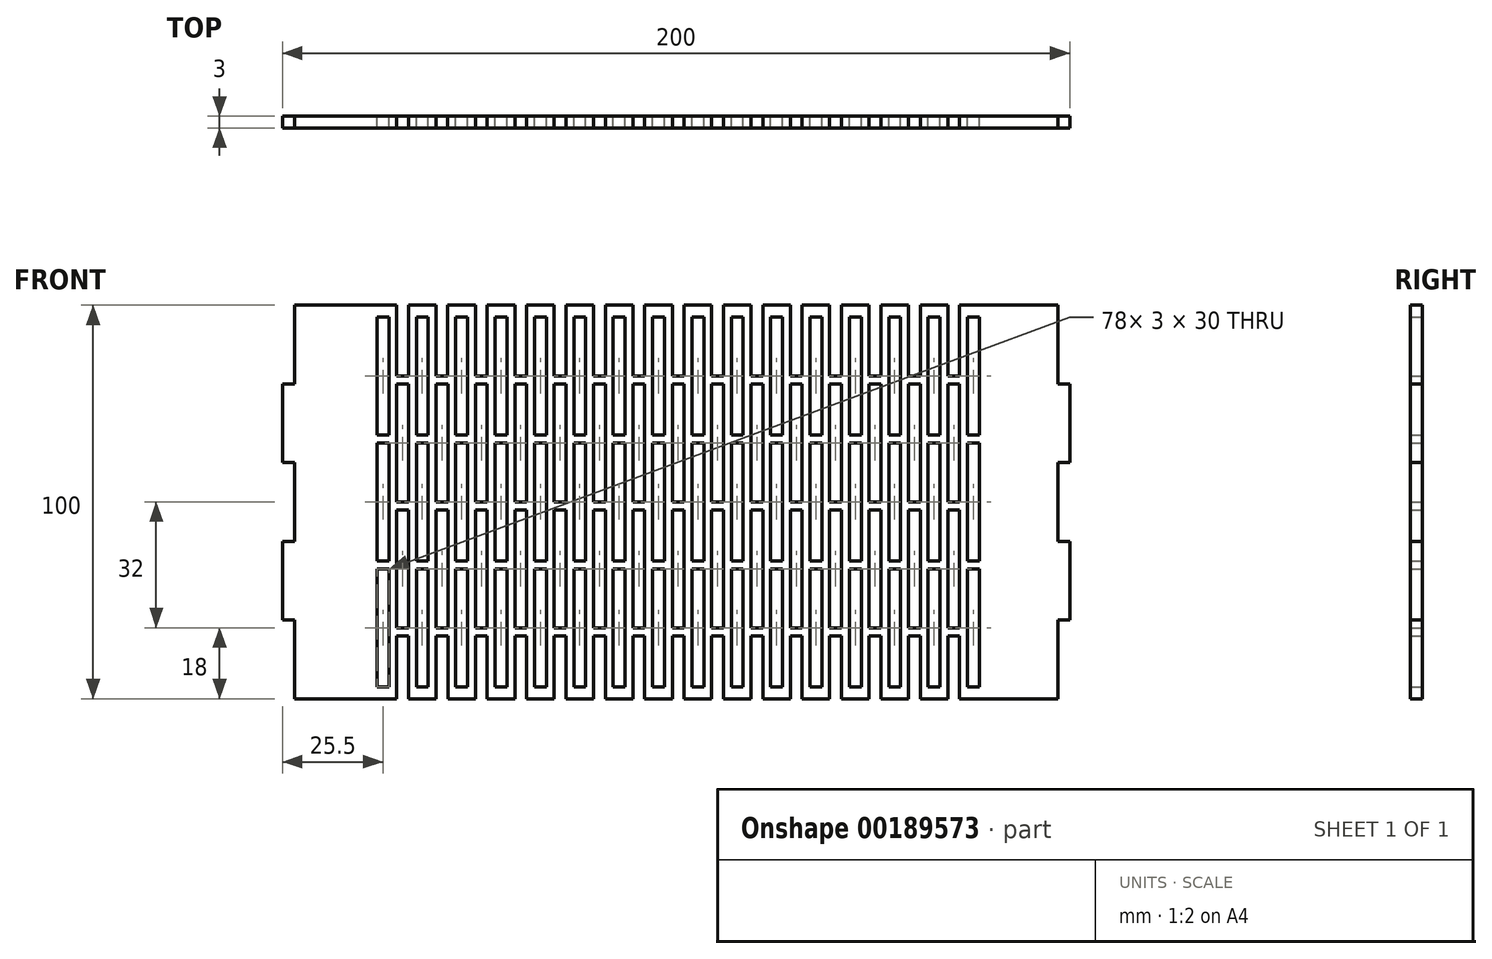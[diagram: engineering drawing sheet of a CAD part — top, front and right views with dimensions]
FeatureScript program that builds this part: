
annotation { "Feature Type Name" : "Feature", "Feature Type Description" : "" }
export const myFeature = defineFeature(function(context is Context, id is Id, definition is map)
    precondition{}
    {
        {
            var Q0;
            Q0=qCreatedBy(makeId("Front.planeOp"),FACE);
            var sketch = newSketch(context, id + "F0", { "sketchPlane" : qUnion([Q0])});
            skLineSegment(sketch, "E0.bottom", {"start": v(80, 50) * mm, "end": v(-80, 50) * mm});
            skLineSegment(sketch, "E0.top", {"start": v(80, -50) * mm, "end": v(-80, -50) * mm});
            skLineSegment(sketch, "E0.left", {"start": v(80, 50) * mm, "end": v(80, -50) * mm});
            skLineSegment(sketch, "E0.right", {"start": v(-80, 50) * mm, "end": v(-80, -50) * mm});
            skPoint(sketch, "E0.middle", {"position": v(0, 0) * mm});
            skLineSegment(sketch, "E1.bottom", {"start": v(-76, 47) * mm, "end": v(-73, 47) * mm});
            skLineSegment(sketch, "E1.top", {"start": v(-76, 17) * mm, "end": v(-73, 17) * mm});
            skLineSegment(sketch, "E1.left", {"start": v(-76, 47) * mm, "end": v(-76, 17) * mm});
            skLineSegment(sketch, "E1.right", {"start": v(-73, 47) * mm, "end": v(-73, 17) * mm});
            skLineSegment(sketch, "E2.0.1.0", {"start": v(-76, -15) * mm, "end": v(-73, -15) * mm});
            skLineSegment(sketch, "E2.0.1.1", {"start": v(-76, 15) * mm, "end": v(-76, -15) * mm});
            skLineSegment(sketch, "E2.0.1.2", {"start": v(-73, 15) * mm, "end": v(-73, -15) * mm});
            skLineSegment(sketch, "E2.0.1.3", {"start": v(-76, 15) * mm, "end": v(-73, 15) * mm});
            skLineSegment(sketch, "E2.0.2.0", {"start": v(-76, -47) * mm, "end": v(-73, -47) * mm});
            skLineSegment(sketch, "E2.0.2.1", {"start": v(-76, -17) * mm, "end": v(-76, -47) * mm});
            skLineSegment(sketch, "E2.0.2.2", {"start": v(-73, -17) * mm, "end": v(-73, -47) * mm});
            skLineSegment(sketch, "E2.0.2.3", {"start": v(-76, -17) * mm, "end": v(-73, -17) * mm});
            skLineSegment(sketch, "E2.1.0.0", {"start": v(-66, 17) * mm, "end": v(-63, 17) * mm});
            skLineSegment(sketch, "E2.1.0.1", {"start": v(-66, 47) * mm, "end": v(-66, 17) * mm});
            skLineSegment(sketch, "E2.1.0.2", {"start": v(-63, 47) * mm, "end": v(-63, 17) * mm});
            skLineSegment(sketch, "E2.1.0.3", {"start": v(-66, 47) * mm, "end": v(-63, 47) * mm});
            skLineSegment(sketch, "E2.1.1.0", {"start": v(-66, -15) * mm, "end": v(-63, -15) * mm});
            skLineSegment(sketch, "E2.1.1.1", {"start": v(-66, 15) * mm, "end": v(-66, -15) * mm});
            skLineSegment(sketch, "E2.1.1.2", {"start": v(-63, 15) * mm, "end": v(-63, -15) * mm});
            skLineSegment(sketch, "E2.1.1.3", {"start": v(-66, 15) * mm, "end": v(-63, 15) * mm});
            skLineSegment(sketch, "E2.1.2.0", {"start": v(-66, -47) * mm, "end": v(-63, -47) * mm});
            skLineSegment(sketch, "E2.1.2.1", {"start": v(-66, -17) * mm, "end": v(-66, -47) * mm});
            skLineSegment(sketch, "E2.1.2.2", {"start": v(-63, -17) * mm, "end": v(-63, -47) * mm});
            skLineSegment(sketch, "E2.1.2.3", {"start": v(-66, -17) * mm, "end": v(-63, -17) * mm});
            skLineSegment(sketch, "E2.2.0.0", {"start": v(-56, 17) * mm, "end": v(-53, 17) * mm});
            skLineSegment(sketch, "E2.2.0.1", {"start": v(-56, 47) * mm, "end": v(-56, 17) * mm});
            skLineSegment(sketch, "E2.2.0.2", {"start": v(-53, 47) * mm, "end": v(-53, 17) * mm});
            skLineSegment(sketch, "E2.2.0.3", {"start": v(-56, 47) * mm, "end": v(-53, 47) * mm});
            skLineSegment(sketch, "E2.2.1.0", {"start": v(-56, -15) * mm, "end": v(-53, -15) * mm});
            skLineSegment(sketch, "E2.2.1.1", {"start": v(-56, 15) * mm, "end": v(-56, -15) * mm});
            skLineSegment(sketch, "E2.2.1.2", {"start": v(-53, 15) * mm, "end": v(-53, -15) * mm});
            skLineSegment(sketch, "E2.2.1.3", {"start": v(-56, 15) * mm, "end": v(-53, 15) * mm});
            skLineSegment(sketch, "E2.2.2.0", {"start": v(-56, -47) * mm, "end": v(-53, -47) * mm});
            skLineSegment(sketch, "E2.2.2.1", {"start": v(-56, -17) * mm, "end": v(-56, -47) * mm});
            skLineSegment(sketch, "E2.2.2.2", {"start": v(-53, -17) * mm, "end": v(-53, -47) * mm});
            skLineSegment(sketch, "E2.2.2.3", {"start": v(-56, -17) * mm, "end": v(-53, -17) * mm});
            skLineSegment(sketch, "E2.3.0.0", {"start": v(-46, 17) * mm, "end": v(-43, 17) * mm});
            skLineSegment(sketch, "E2.3.0.1", {"start": v(-46, 47) * mm, "end": v(-46, 17) * mm});
            skLineSegment(sketch, "E2.3.0.2", {"start": v(-43, 47) * mm, "end": v(-43, 17) * mm});
            skLineSegment(sketch, "E2.3.0.3", {"start": v(-46, 47) * mm, "end": v(-43, 47) * mm});
            skLineSegment(sketch, "E2.3.1.0", {"start": v(-46, -15) * mm, "end": v(-43, -15) * mm});
            skLineSegment(sketch, "E2.3.1.1", {"start": v(-46, 15) * mm, "end": v(-46, -15) * mm});
            skLineSegment(sketch, "E2.3.1.2", {"start": v(-43, 15) * mm, "end": v(-43, -15) * mm});
            skLineSegment(sketch, "E2.3.1.3", {"start": v(-46, 15) * mm, "end": v(-43, 15) * mm});
            skLineSegment(sketch, "E2.3.2.0", {"start": v(-46, -47) * mm, "end": v(-43, -47) * mm});
            skLineSegment(sketch, "E2.3.2.1", {"start": v(-46, -17) * mm, "end": v(-46, -47) * mm});
            skLineSegment(sketch, "E2.3.2.2", {"start": v(-43, -17) * mm, "end": v(-43, -47) * mm});
            skLineSegment(sketch, "E2.3.2.3", {"start": v(-46, -17) * mm, "end": v(-43, -17) * mm});
            skLineSegment(sketch, "E2.4.0.0", {"start": v(-36, 17) * mm, "end": v(-33, 17) * mm});
            skLineSegment(sketch, "E2.4.0.1", {"start": v(-36, 47) * mm, "end": v(-36, 17) * mm});
            skLineSegment(sketch, "E2.4.0.2", {"start": v(-33, 47) * mm, "end": v(-33, 17) * mm});
            skLineSegment(sketch, "E2.4.0.3", {"start": v(-36, 47) * mm, "end": v(-33, 47) * mm});
            skLineSegment(sketch, "E2.4.1.0", {"start": v(-36, -15) * mm, "end": v(-33, -15) * mm});
            skLineSegment(sketch, "E2.4.1.1", {"start": v(-36, 15) * mm, "end": v(-36, -15) * mm});
            skLineSegment(sketch, "E2.4.1.2", {"start": v(-33, 15) * mm, "end": v(-33, -15) * mm});
            skLineSegment(sketch, "E2.4.1.3", {"start": v(-36, 15) * mm, "end": v(-33, 15) * mm});
            skLineSegment(sketch, "E2.4.2.0", {"start": v(-36, -47) * mm, "end": v(-33, -47) * mm});
            skLineSegment(sketch, "E2.4.2.1", {"start": v(-36, -17) * mm, "end": v(-36, -47) * mm});
            skLineSegment(sketch, "E2.4.2.2", {"start": v(-33, -17) * mm, "end": v(-33, -47) * mm});
            skLineSegment(sketch, "E2.4.2.3", {"start": v(-36, -17) * mm, "end": v(-33, -17) * mm});
            skLineSegment(sketch, "E2.5.0.0", {"start": v(-26, 17) * mm, "end": v(-23, 17) * mm});
            skLineSegment(sketch, "E2.5.0.1", {"start": v(-26, 47) * mm, "end": v(-26, 17) * mm});
            skLineSegment(sketch, "E2.5.0.2", {"start": v(-23, 47) * mm, "end": v(-23, 17) * mm});
            skLineSegment(sketch, "E2.5.0.3", {"start": v(-26, 47) * mm, "end": v(-23, 47) * mm});
            skLineSegment(sketch, "E2.5.1.0", {"start": v(-26, -15) * mm, "end": v(-23, -15) * mm});
            skLineSegment(sketch, "E2.5.1.1", {"start": v(-26, 15) * mm, "end": v(-26, -15) * mm});
            skLineSegment(sketch, "E2.5.1.2", {"start": v(-23, 15) * mm, "end": v(-23, -15) * mm});
            skLineSegment(sketch, "E2.5.1.3", {"start": v(-26, 15) * mm, "end": v(-23, 15) * mm});
            skLineSegment(sketch, "E2.5.2.0", {"start": v(-26, -47) * mm, "end": v(-23, -47) * mm});
            skLineSegment(sketch, "E2.5.2.1", {"start": v(-26, -17) * mm, "end": v(-26, -47) * mm});
            skLineSegment(sketch, "E2.5.2.2", {"start": v(-23, -17) * mm, "end": v(-23, -47) * mm});
            skLineSegment(sketch, "E2.5.2.3", {"start": v(-26, -17) * mm, "end": v(-23, -17) * mm});
            skLineSegment(sketch, "E2.6.0.0", {"start": v(-16, 17) * mm, "end": v(-13, 17) * mm});
            skLineSegment(sketch, "E2.6.0.1", {"start": v(-16, 47) * mm, "end": v(-16, 17) * mm});
            skLineSegment(sketch, "E2.6.0.2", {"start": v(-13, 47) * mm, "end": v(-13, 17) * mm});
            skLineSegment(sketch, "E2.6.0.3", {"start": v(-16, 47) * mm, "end": v(-13, 47) * mm});
            skLineSegment(sketch, "E2.6.1.0", {"start": v(-16, -15) * mm, "end": v(-13, -15) * mm});
            skLineSegment(sketch, "E2.6.1.1", {"start": v(-16, 15) * mm, "end": v(-16, -15) * mm});
            skLineSegment(sketch, "E2.6.1.2", {"start": v(-13, 15) * mm, "end": v(-13, -15) * mm});
            skLineSegment(sketch, "E2.6.1.3", {"start": v(-16, 15) * mm, "end": v(-13, 15) * mm});
            skLineSegment(sketch, "E2.6.2.0", {"start": v(-16, -47) * mm, "end": v(-13, -47) * mm});
            skLineSegment(sketch, "E2.6.2.1", {"start": v(-16, -17) * mm, "end": v(-16, -47) * mm});
            skLineSegment(sketch, "E2.6.2.2", {"start": v(-13, -17) * mm, "end": v(-13, -47) * mm});
            skLineSegment(sketch, "E2.6.2.3", {"start": v(-16, -17) * mm, "end": v(-13, -17) * mm});
            skLineSegment(sketch, "E2.7.0.0", {"start": v(-6, 17) * mm, "end": v(-3, 17) * mm});
            skLineSegment(sketch, "E2.7.0.1", {"start": v(-6, 47) * mm, "end": v(-6, 17) * mm});
            skLineSegment(sketch, "E2.7.0.2", {"start": v(-3, 47) * mm, "end": v(-3, 17) * mm});
            skLineSegment(sketch, "E2.7.0.3", {"start": v(-6, 47) * mm, "end": v(-3, 47) * mm});
            skLineSegment(sketch, "E2.7.1.0", {"start": v(-6, -15) * mm, "end": v(-3, -15) * mm});
            skLineSegment(sketch, "E2.7.1.1", {"start": v(-6, 15) * mm, "end": v(-6, -15) * mm});
            skLineSegment(sketch, "E2.7.1.2", {"start": v(-3, 15) * mm, "end": v(-3, -15) * mm});
            skLineSegment(sketch, "E2.7.1.3", {"start": v(-6, 15) * mm, "end": v(-3, 15) * mm});
            skLineSegment(sketch, "E2.7.2.0", {"start": v(-6, -47) * mm, "end": v(-3, -47) * mm});
            skLineSegment(sketch, "E2.7.2.1", {"start": v(-6, -17) * mm, "end": v(-6, -47) * mm});
            skLineSegment(sketch, "E2.7.2.2", {"start": v(-3, -17) * mm, "end": v(-3, -47) * mm});
            skLineSegment(sketch, "E2.7.2.3", {"start": v(-6, -17) * mm, "end": v(-3, -17) * mm});
            skLineSegment(sketch, "E2.8.0.0", {"start": v(4, 17) * mm, "end": v(7, 17) * mm});
            skLineSegment(sketch, "E2.8.0.1", {"start": v(4, 47) * mm, "end": v(4, 17) * mm});
            skLineSegment(sketch, "E2.8.0.2", {"start": v(7, 47) * mm, "end": v(7, 17) * mm});
            skLineSegment(sketch, "E2.8.0.3", {"start": v(4, 47) * mm, "end": v(7, 47) * mm});
            skLineSegment(sketch, "E2.8.1.0", {"start": v(4, -15) * mm, "end": v(7, -15) * mm});
            skLineSegment(sketch, "E2.8.1.1", {"start": v(4, 15) * mm, "end": v(4, -15) * mm});
            skLineSegment(sketch, "E2.8.1.2", {"start": v(7, 15) * mm, "end": v(7, -15) * mm});
            skLineSegment(sketch, "E2.8.1.3", {"start": v(4, 15) * mm, "end": v(7, 15) * mm});
            skLineSegment(sketch, "E2.8.2.0", {"start": v(4, -47) * mm, "end": v(7, -47) * mm});
            skLineSegment(sketch, "E2.8.2.1", {"start": v(4, -17) * mm, "end": v(4, -47) * mm});
            skLineSegment(sketch, "E2.8.2.2", {"start": v(7, -17) * mm, "end": v(7, -47) * mm});
            skLineSegment(sketch, "E2.8.2.3", {"start": v(4, -17) * mm, "end": v(7, -17) * mm});
            skLineSegment(sketch, "E2.9.0.0", {"start": v(14, 17) * mm, "end": v(17, 17) * mm});
            skLineSegment(sketch, "E2.9.0.1", {"start": v(14, 47) * mm, "end": v(14, 17) * mm});
            skLineSegment(sketch, "E2.9.0.2", {"start": v(17, 47) * mm, "end": v(17, 17) * mm});
            skLineSegment(sketch, "E2.9.0.3", {"start": v(14, 47) * mm, "end": v(17, 47) * mm});
            skLineSegment(sketch, "E2.9.1.0", {"start": v(14, -15) * mm, "end": v(17, -15) * mm});
            skLineSegment(sketch, "E2.9.1.1", {"start": v(14, 15) * mm, "end": v(14, -15) * mm});
            skLineSegment(sketch, "E2.9.1.2", {"start": v(17, 15) * mm, "end": v(17, -15) * mm});
            skLineSegment(sketch, "E2.9.1.3", {"start": v(14, 15) * mm, "end": v(17, 15) * mm});
            skLineSegment(sketch, "E2.9.2.0", {"start": v(14, -47) * mm, "end": v(17, -47) * mm});
            skLineSegment(sketch, "E2.9.2.1", {"start": v(14, -17) * mm, "end": v(14, -47) * mm});
            skLineSegment(sketch, "E2.9.2.2", {"start": v(17, -17) * mm, "end": v(17, -47) * mm});
            skLineSegment(sketch, "E2.9.2.3", {"start": v(14, -17) * mm, "end": v(17, -17) * mm});
            skLineSegment(sketch, "E2.10.0.0", {"start": v(24, 17) * mm, "end": v(27, 17) * mm});
            skLineSegment(sketch, "E2.10.0.1", {"start": v(24, 47) * mm, "end": v(24, 17) * mm});
            skLineSegment(sketch, "E2.10.0.2", {"start": v(27, 47) * mm, "end": v(27, 17) * mm});
            skLineSegment(sketch, "E2.10.0.3", {"start": v(24, 47) * mm, "end": v(27, 47) * mm});
            skLineSegment(sketch, "E2.10.1.0", {"start": v(24, -15) * mm, "end": v(27, -15) * mm});
            skLineSegment(sketch, "E2.10.1.1", {"start": v(24, 15) * mm, "end": v(24, -15) * mm});
            skLineSegment(sketch, "E2.10.1.2", {"start": v(27, 15) * mm, "end": v(27, -15) * mm});
            skLineSegment(sketch, "E2.10.1.3", {"start": v(24, 15) * mm, "end": v(27, 15) * mm});
            skLineSegment(sketch, "E2.10.2.0", {"start": v(24, -47) * mm, "end": v(27, -47) * mm});
            skLineSegment(sketch, "E2.10.2.1", {"start": v(24, -17) * mm, "end": v(24, -47) * mm});
            skLineSegment(sketch, "E2.10.2.2", {"start": v(27, -17) * mm, "end": v(27, -47) * mm});
            skLineSegment(sketch, "E2.10.2.3", {"start": v(24, -17) * mm, "end": v(27, -17) * mm});
            skLineSegment(sketch, "E2.11.0.0", {"start": v(34, 17) * mm, "end": v(37, 17) * mm});
            skLineSegment(sketch, "E2.11.0.1", {"start": v(34, 47) * mm, "end": v(34, 17) * mm});
            skLineSegment(sketch, "E2.11.0.2", {"start": v(37, 47) * mm, "end": v(37, 17) * mm});
            skLineSegment(sketch, "E2.11.0.3", {"start": v(34, 47) * mm, "end": v(37, 47) * mm});
            skLineSegment(sketch, "E2.11.1.0", {"start": v(34, -15) * mm, "end": v(37, -15) * mm});
            skLineSegment(sketch, "E2.11.1.1", {"start": v(34, 15) * mm, "end": v(34, -15) * mm});
            skLineSegment(sketch, "E2.11.1.2", {"start": v(37, 15) * mm, "end": v(37, -15) * mm});
            skLineSegment(sketch, "E2.11.1.3", {"start": v(34, 15) * mm, "end": v(37, 15) * mm});
            skLineSegment(sketch, "E2.11.2.0", {"start": v(34, -47) * mm, "end": v(37, -47) * mm});
            skLineSegment(sketch, "E2.11.2.1", {"start": v(34, -17) * mm, "end": v(34, -47) * mm});
            skLineSegment(sketch, "E2.11.2.2", {"start": v(37, -17) * mm, "end": v(37, -47) * mm});
            skLineSegment(sketch, "E2.11.2.3", {"start": v(34, -17) * mm, "end": v(37, -17) * mm});
            skLineSegment(sketch, "E2.12.0.0", {"start": v(44, 17) * mm, "end": v(47, 17) * mm});
            skLineSegment(sketch, "E2.12.0.1", {"start": v(44, 47) * mm, "end": v(44, 17) * mm});
            skLineSegment(sketch, "E2.12.0.2", {"start": v(47, 47) * mm, "end": v(47, 17) * mm});
            skLineSegment(sketch, "E2.12.0.3", {"start": v(44, 47) * mm, "end": v(47, 47) * mm});
            skLineSegment(sketch, "E2.12.1.0", {"start": v(44, -15) * mm, "end": v(47, -15) * mm});
            skLineSegment(sketch, "E2.12.1.1", {"start": v(44, 15) * mm, "end": v(44, -15) * mm});
            skLineSegment(sketch, "E2.12.1.2", {"start": v(47, 15) * mm, "end": v(47, -15) * mm});
            skLineSegment(sketch, "E2.12.1.3", {"start": v(44, 15) * mm, "end": v(47, 15) * mm});
            skLineSegment(sketch, "E2.12.2.0", {"start": v(44, -47) * mm, "end": v(47, -47) * mm});
            skLineSegment(sketch, "E2.12.2.1", {"start": v(44, -17) * mm, "end": v(44, -47) * mm});
            skLineSegment(sketch, "E2.12.2.2", {"start": v(47, -17) * mm, "end": v(47, -47) * mm});
            skLineSegment(sketch, "E2.12.2.3", {"start": v(44, -17) * mm, "end": v(47, -17) * mm});
            skLineSegment(sketch, "E2.13.0.0", {"start": v(54, 17) * mm, "end": v(57, 17) * mm});
            skLineSegment(sketch, "E2.13.0.1", {"start": v(54, 47) * mm, "end": v(54, 17) * mm});
            skLineSegment(sketch, "E2.13.0.2", {"start": v(57, 47) * mm, "end": v(57, 17) * mm});
            skLineSegment(sketch, "E2.13.0.3", {"start": v(54, 47) * mm, "end": v(57, 47) * mm});
            skLineSegment(sketch, "E2.13.1.0", {"start": v(54, -15) * mm, "end": v(57, -15) * mm});
            skLineSegment(sketch, "E2.13.1.1", {"start": v(54, 15) * mm, "end": v(54, -15) * mm});
            skLineSegment(sketch, "E2.13.1.2", {"start": v(57, 15) * mm, "end": v(57, -15) * mm});
            skLineSegment(sketch, "E2.13.1.3", {"start": v(54, 15) * mm, "end": v(57, 15) * mm});
            skLineSegment(sketch, "E2.13.2.0", {"start": v(54, -47) * mm, "end": v(57, -47) * mm});
            skLineSegment(sketch, "E2.13.2.1", {"start": v(54, -17) * mm, "end": v(54, -47) * mm});
            skLineSegment(sketch, "E2.13.2.2", {"start": v(57, -17) * mm, "end": v(57, -47) * mm});
            skLineSegment(sketch, "E2.13.2.3", {"start": v(54, -17) * mm, "end": v(57, -17) * mm});
            skLineSegment(sketch, "E2.14.0.0", {"start": v(64, 17) * mm, "end": v(67, 17) * mm});
            skLineSegment(sketch, "E2.14.0.1", {"start": v(64, 47) * mm, "end": v(64, 17) * mm});
            skLineSegment(sketch, "E2.14.0.2", {"start": v(67, 47) * mm, "end": v(67, 17) * mm});
            skLineSegment(sketch, "E2.14.0.3", {"start": v(64, 47) * mm, "end": v(67, 47) * mm});
            skLineSegment(sketch, "E2.14.1.0", {"start": v(64, -15) * mm, "end": v(67, -15) * mm});
            skLineSegment(sketch, "E2.14.1.1", {"start": v(64, 15) * mm, "end": v(64, -15) * mm});
            skLineSegment(sketch, "E2.14.1.2", {"start": v(67, 15) * mm, "end": v(67, -15) * mm});
            skLineSegment(sketch, "E2.14.1.3", {"start": v(64, 15) * mm, "end": v(67, 15) * mm});
            skLineSegment(sketch, "E2.14.2.0", {"start": v(64, -47) * mm, "end": v(67, -47) * mm});
            skLineSegment(sketch, "E2.14.2.1", {"start": v(64, -17) * mm, "end": v(64, -47) * mm});
            skLineSegment(sketch, "E2.14.2.2", {"start": v(67, -17) * mm, "end": v(67, -47) * mm});
            skLineSegment(sketch, "E2.14.2.3", {"start": v(64, -17) * mm, "end": v(67, -17) * mm});
            skLineSegment(sketch, "E2.direction1", {"start": v(-76, 17) * mm, "end": v(-66, 17) * mm, "construction": true});
            skLineSegment(sketch, "E2.direction2", {"start": v(-76, 17) * mm, "end": v(-76, -15) * mm, "construction": true});
            skLineSegment(sketch, "E3.0.15.0", {"start": v(74, 17) * mm, "end": v(77, 17) * mm});
            skLineSegment(sketch, "E3.3.15.0", {"start": v(74, 47) * mm, "end": v(74, 17) * mm});
            skLineSegment(sketch, "E3.6.15.0", {"start": v(77, 47) * mm, "end": v(77, 17) * mm});
            skLineSegment(sketch, "E3.9.15.0", {"start": v(74, 47) * mm, "end": v(77, 47) * mm});
            skLineSegment(sketch, "E3.0.15.1", {"start": v(74, -15) * mm, "end": v(77, -15) * mm});
            skLineSegment(sketch, "E3.3.15.1", {"start": v(74, 15) * mm, "end": v(74, -15) * mm});
            skLineSegment(sketch, "E3.6.15.1", {"start": v(77, 15) * mm, "end": v(77, -15) * mm});
            skLineSegment(sketch, "E3.9.15.1", {"start": v(74, 15) * mm, "end": v(77, 15) * mm});
            skLineSegment(sketch, "E3.0.15.2", {"start": v(74, -47) * mm, "end": v(77, -47) * mm});
            skLineSegment(sketch, "E3.3.15.2", {"start": v(74, -17) * mm, "end": v(74, -47) * mm});
            skLineSegment(sketch, "E3.6.15.2", {"start": v(77, -17) * mm, "end": v(77, -47) * mm});
            skLineSegment(sketch, "E3.9.15.2", {"start": v(74, -17) * mm, "end": v(77, -17) * mm});
            skLineSegment(sketch, "E4.bottom", {"start": v(72, 30) * mm, "end": v(69, 30) * mm});
            skLineSegment(sketch, "E4.top", {"start": v(72, 0) * mm, "end": v(69, 0) * mm});
            skLineSegment(sketch, "E4.left", {"start": v(72, 30) * mm, "end": v(72, 0) * mm});
            skLineSegment(sketch, "E4.right", {"start": v(69, 30) * mm, "end": v(69, 0) * mm});
            skLineSegment(sketch, "E5.bottom", {"start": v(72, 32) * mm, "end": v(69, 32) * mm});
            skLineSegment(sketch, "E5.top", {"start": v(72, 47) * mm, "end": v(69, 47) * mm, "construction": true});
            skLineSegment(sketch, "E5.left", {"start": v(72, 32) * mm, "end": v(72, 47) * mm});
            skLineSegment(sketch, "E5.right", {"start": v(69, 32) * mm, "end": v(69, 47) * mm});
            skLineSegment(sketch, "E6.1.0.0", {"start": v(59, 32) * mm, "end": v(59, 47) * mm});
            skLineSegment(sketch, "E6.1.0.1", {"start": v(62, 47) * mm, "end": v(59, 47) * mm, "construction": true});
            skLineSegment(sketch, "E6.1.0.2", {"start": v(62, 32) * mm, "end": v(62, 47) * mm});
            skLineSegment(sketch, "E6.1.0.3", {"start": v(62, 32) * mm, "end": v(59, 32) * mm});
            skLineSegment(sketch, "E6.1.0.4", {"start": v(62, 30) * mm, "end": v(59, 30) * mm});
            skLineSegment(sketch, "E6.1.0.5", {"start": v(59, 30) * mm, "end": v(59, 0) * mm});
            skLineSegment(sketch, "E6.1.0.6", {"start": v(62, 30) * mm, "end": v(62, 0) * mm});
            skLineSegment(sketch, "E6.1.0.7", {"start": v(62, 0) * mm, "end": v(59, 0) * mm});
            skLineSegment(sketch, "E6.2.0.0", {"start": v(49, 32) * mm, "end": v(49, 47) * mm});
            skLineSegment(sketch, "E6.2.0.1", {"start": v(52, 47) * mm, "end": v(49, 47) * mm, "construction": true});
            skLineSegment(sketch, "E6.2.0.2", {"start": v(52, 32) * mm, "end": v(52, 47) * mm});
            skLineSegment(sketch, "E6.2.0.3", {"start": v(52, 32) * mm, "end": v(49, 32) * mm});
            skLineSegment(sketch, "E6.2.0.4", {"start": v(52, 30) * mm, "end": v(49, 30) * mm});
            skLineSegment(sketch, "E6.2.0.5", {"start": v(49, 30) * mm, "end": v(49, 0) * mm});
            skLineSegment(sketch, "E6.2.0.6", {"start": v(52, 30) * mm, "end": v(52, 0) * mm});
            skLineSegment(sketch, "E6.2.0.7", {"start": v(52, 0) * mm, "end": v(49, 0) * mm});
            skLineSegment(sketch, "E6.3.0.0", {"start": v(39, 32) * mm, "end": v(39, 47) * mm});
            skLineSegment(sketch, "E6.3.0.1", {"start": v(42, 47) * mm, "end": v(39, 47) * mm, "construction": true});
            skLineSegment(sketch, "E6.3.0.2", {"start": v(42, 32) * mm, "end": v(42, 47) * mm});
            skLineSegment(sketch, "E6.3.0.3", {"start": v(42, 32) * mm, "end": v(39, 32) * mm});
            skLineSegment(sketch, "E6.3.0.4", {"start": v(42, 30) * mm, "end": v(39, 30) * mm});
            skLineSegment(sketch, "E6.3.0.5", {"start": v(39, 30) * mm, "end": v(39, 0) * mm});
            skLineSegment(sketch, "E6.3.0.6", {"start": v(42, 30) * mm, "end": v(42, 0) * mm});
            skLineSegment(sketch, "E6.3.0.7", {"start": v(42, 0) * mm, "end": v(39, 0) * mm});
            skLineSegment(sketch, "E6.4.0.0", {"start": v(29, 32) * mm, "end": v(29, 47) * mm});
            skLineSegment(sketch, "E6.4.0.1", {"start": v(32, 47) * mm, "end": v(29, 47) * mm, "construction": true});
            skLineSegment(sketch, "E6.4.0.2", {"start": v(32, 32) * mm, "end": v(32, 47) * mm});
            skLineSegment(sketch, "E6.4.0.3", {"start": v(32, 32) * mm, "end": v(29, 32) * mm});
            skLineSegment(sketch, "E6.4.0.4", {"start": v(32, 30) * mm, "end": v(29, 30) * mm});
            skLineSegment(sketch, "E6.4.0.5", {"start": v(29, 30) * mm, "end": v(29, 0) * mm});
            skLineSegment(sketch, "E6.4.0.6", {"start": v(32, 30) * mm, "end": v(32, 0) * mm});
            skLineSegment(sketch, "E6.4.0.7", {"start": v(32, 0) * mm, "end": v(29, 0) * mm});
            skLineSegment(sketch, "E6.5.0.0", {"start": v(19, 32) * mm, "end": v(19, 47) * mm});
            skLineSegment(sketch, "E6.5.0.1", {"start": v(22, 47) * mm, "end": v(19, 47) * mm, "construction": true});
            skLineSegment(sketch, "E6.5.0.2", {"start": v(22, 32) * mm, "end": v(22, 47) * mm});
            skLineSegment(sketch, "E6.5.0.3", {"start": v(22, 32) * mm, "end": v(19, 32) * mm});
            skLineSegment(sketch, "E6.5.0.4", {"start": v(22, 30) * mm, "end": v(19, 30) * mm});
            skLineSegment(sketch, "E6.5.0.5", {"start": v(19, 30) * mm, "end": v(19, 0) * mm});
            skLineSegment(sketch, "E6.5.0.6", {"start": v(22, 30) * mm, "end": v(22, 0) * mm});
            skLineSegment(sketch, "E6.5.0.7", {"start": v(22, 0) * mm, "end": v(19, 0) * mm});
            skLineSegment(sketch, "E6.6.0.0", {"start": v(9, 32) * mm, "end": v(9, 47) * mm});
            skLineSegment(sketch, "E6.6.0.1", {"start": v(12, 47) * mm, "end": v(9, 47) * mm, "construction": true});
            skLineSegment(sketch, "E6.6.0.2", {"start": v(12, 32) * mm, "end": v(12, 47) * mm});
            skLineSegment(sketch, "E6.6.0.3", {"start": v(12, 32) * mm, "end": v(9, 32) * mm});
            skLineSegment(sketch, "E6.6.0.4", {"start": v(12, 30) * mm, "end": v(9, 30) * mm});
            skLineSegment(sketch, "E6.6.0.5", {"start": v(9, 30) * mm, "end": v(9, 0) * mm});
            skLineSegment(sketch, "E6.6.0.6", {"start": v(12, 30) * mm, "end": v(12, 0) * mm});
            skLineSegment(sketch, "E6.6.0.7", {"start": v(12, 0) * mm, "end": v(9, 0) * mm});
            skLineSegment(sketch, "E6.7.0.0", {"start": v(-1, 32) * mm, "end": v(-1, 47) * mm});
            skLineSegment(sketch, "E6.7.0.1", {"start": v(2, 47) * mm, "end": v(-1, 47) * mm, "construction": true});
            skLineSegment(sketch, "E6.7.0.2", {"start": v(2, 32) * mm, "end": v(2, 47) * mm});
            skLineSegment(sketch, "E6.7.0.3", {"start": v(2, 32) * mm, "end": v(-1, 32) * mm});
            skLineSegment(sketch, "E6.7.0.4", {"start": v(2, 30) * mm, "end": v(-1, 30) * mm});
            skLineSegment(sketch, "E6.7.0.5", {"start": v(-1, 30) * mm, "end": v(-1, 0) * mm});
            skLineSegment(sketch, "E6.7.0.6", {"start": v(2, 30) * mm, "end": v(2, 0) * mm});
            skLineSegment(sketch, "E6.7.0.7", {"start": v(2, 0) * mm, "end": v(-1, 0) * mm});
            skLineSegment(sketch, "E6.8.0.0", {"start": v(-11, 32) * mm, "end": v(-11, 47) * mm});
            skLineSegment(sketch, "E6.8.0.1", {"start": v(-8, 47) * mm, "end": v(-11, 47) * mm, "construction": true});
            skLineSegment(sketch, "E6.8.0.2", {"start": v(-8, 32) * mm, "end": v(-8, 47) * mm});
            skLineSegment(sketch, "E6.8.0.3", {"start": v(-8, 32) * mm, "end": v(-11, 32) * mm});
            skLineSegment(sketch, "E6.8.0.4", {"start": v(-8, 30) * mm, "end": v(-11, 30) * mm});
            skLineSegment(sketch, "E6.8.0.5", {"start": v(-11, 30) * mm, "end": v(-11, 0) * mm});
            skLineSegment(sketch, "E6.8.0.6", {"start": v(-8, 30) * mm, "end": v(-8, 0) * mm});
            skLineSegment(sketch, "E6.8.0.7", {"start": v(-8, 0) * mm, "end": v(-11, 0) * mm});
            skLineSegment(sketch, "E6.9.0.0", {"start": v(-21, 32) * mm, "end": v(-21, 47) * mm});
            skLineSegment(sketch, "E6.9.0.1", {"start": v(-18, 47) * mm, "end": v(-21, 47) * mm, "construction": true});
            skLineSegment(sketch, "E6.9.0.2", {"start": v(-18, 32) * mm, "end": v(-18, 47) * mm});
            skLineSegment(sketch, "E6.9.0.3", {"start": v(-18, 32) * mm, "end": v(-21, 32) * mm});
            skLineSegment(sketch, "E6.9.0.4", {"start": v(-18, 30) * mm, "end": v(-21, 30) * mm});
            skLineSegment(sketch, "E6.9.0.5", {"start": v(-21, 30) * mm, "end": v(-21, 0) * mm});
            skLineSegment(sketch, "E6.9.0.6", {"start": v(-18, 30) * mm, "end": v(-18, 0) * mm});
            skLineSegment(sketch, "E6.9.0.7", {"start": v(-18, 0) * mm, "end": v(-21, 0) * mm});
            skLineSegment(sketch, "E6.10.0.0", {"start": v(-31, 32) * mm, "end": v(-31, 47) * mm});
            skLineSegment(sketch, "E6.10.0.1", {"start": v(-28, 47) * mm, "end": v(-31, 47) * mm, "construction": true});
            skLineSegment(sketch, "E6.10.0.2", {"start": v(-28, 32) * mm, "end": v(-28, 47) * mm});
            skLineSegment(sketch, "E6.10.0.3", {"start": v(-28, 32) * mm, "end": v(-31, 32) * mm});
            skLineSegment(sketch, "E6.10.0.4", {"start": v(-28, 30) * mm, "end": v(-31, 30) * mm});
            skLineSegment(sketch, "E6.10.0.5", {"start": v(-31, 30) * mm, "end": v(-31, 0) * mm});
            skLineSegment(sketch, "E6.10.0.6", {"start": v(-28, 30) * mm, "end": v(-28, 0) * mm});
            skLineSegment(sketch, "E6.10.0.7", {"start": v(-28, 0) * mm, "end": v(-31, 0) * mm});
            skLineSegment(sketch, "E6.11.0.0", {"start": v(-41, 32) * mm, "end": v(-41, 47) * mm});
            skLineSegment(sketch, "E6.11.0.1", {"start": v(-38, 47) * mm, "end": v(-41, 47) * mm, "construction": true});
            skLineSegment(sketch, "E6.11.0.2", {"start": v(-38, 32) * mm, "end": v(-38, 47) * mm});
            skLineSegment(sketch, "E6.11.0.3", {"start": v(-38, 32) * mm, "end": v(-41, 32) * mm});
            skLineSegment(sketch, "E6.11.0.4", {"start": v(-38, 30) * mm, "end": v(-41, 30) * mm});
            skLineSegment(sketch, "E6.11.0.5", {"start": v(-41, 30) * mm, "end": v(-41, 0) * mm});
            skLineSegment(sketch, "E6.11.0.6", {"start": v(-38, 30) * mm, "end": v(-38, 0) * mm});
            skLineSegment(sketch, "E6.11.0.7", {"start": v(-38, 0) * mm, "end": v(-41, 0) * mm});
            skLineSegment(sketch, "E6.12.0.0", {"start": v(-51, 32) * mm, "end": v(-51, 47) * mm});
            skLineSegment(sketch, "E6.12.0.1", {"start": v(-48, 47) * mm, "end": v(-51, 47) * mm, "construction": true});
            skLineSegment(sketch, "E6.12.0.2", {"start": v(-48, 32) * mm, "end": v(-48, 47) * mm});
            skLineSegment(sketch, "E6.12.0.3", {"start": v(-48, 32) * mm, "end": v(-51, 32) * mm});
            skLineSegment(sketch, "E6.12.0.4", {"start": v(-48, 30) * mm, "end": v(-51, 30) * mm});
            skLineSegment(sketch, "E6.12.0.5", {"start": v(-51, 30) * mm, "end": v(-51, 0) * mm});
            skLineSegment(sketch, "E6.12.0.6", {"start": v(-48, 30) * mm, "end": v(-48, 0) * mm});
            skLineSegment(sketch, "E6.12.0.7", {"start": v(-48, 0) * mm, "end": v(-51, 0) * mm});
            skLineSegment(sketch, "E6.13.0.0", {"start": v(-61, 32) * mm, "end": v(-61, 47) * mm});
            skLineSegment(sketch, "E6.13.0.1", {"start": v(-58.03, 47) * mm, "end": v(-61, 47) * mm, "construction": true});
            skLineSegment(sketch, "E6.13.0.2", {"start": v(-58.03, 32) * mm, "end": v(-58.03, 47) * mm});
            skLineSegment(sketch, "E6.13.0.3", {"start": v(-58.03, 32) * mm, "end": v(-61, 32) * mm});
            skLineSegment(sketch, "E6.13.0.4", {"start": v(-58, 30) * mm, "end": v(-61, 30) * mm});
            skLineSegment(sketch, "E6.13.0.5", {"start": v(-61, 30) * mm, "end": v(-61, 0) * mm});
            skLineSegment(sketch, "E6.13.0.6", {"start": v(-58, 30) * mm, "end": v(-58, 0) * mm});
            skLineSegment(sketch, "E6.13.0.7", {"start": v(-58, 0) * mm, "end": v(-61, 0) * mm});
            skLineSegment(sketch, "E6.14.0.0", {"start": v(-71, 32) * mm, "end": v(-71, 47) * mm});
            skLineSegment(sketch, "E6.14.0.1", {"start": v(-68, 47) * mm, "end": v(-71, 47) * mm, "construction": true});
            skLineSegment(sketch, "E6.14.0.2", {"start": v(-68, 32) * mm, "end": v(-68, 47) * mm});
            skLineSegment(sketch, "E6.14.0.3", {"start": v(-68, 32) * mm, "end": v(-71, 32) * mm});
            skLineSegment(sketch, "E6.14.0.4", {"start": v(-68, 30) * mm, "end": v(-71, 30) * mm});
            skLineSegment(sketch, "E6.14.0.5", {"start": v(-71, 30) * mm, "end": v(-71, 0) * mm});
            skLineSegment(sketch, "E6.14.0.6", {"start": v(-68, 30) * mm, "end": v(-68, 0) * mm});
            skLineSegment(sketch, "E6.14.0.7", {"start": v(-68, 0) * mm, "end": v(-71, 0) * mm});
            skLineSegment(sketch, "E6.direction1", {"start": v(69, 32) * mm, "end": v(59, 32) * mm, "construction": true});
            skLineSegment(sketch, "E7.bottom", {"start": v(72, -2) * mm, "end": v(69, -2) * mm});
            skLineSegment(sketch, "E7.top", {"start": v(72, -32) * mm, "end": v(69, -32) * mm});
            skLineSegment(sketch, "E7.left", {"start": v(72, -2) * mm, "end": v(72, -32) * mm});
            skLineSegment(sketch, "E7.right", {"start": v(69, -2) * mm, "end": v(69, -32) * mm});
            skLineSegment(sketch, "E8.bottom", {"start": v(72, -34) * mm, "end": v(69, -34) * mm});
            skLineSegment(sketch, "E8.top", {"start": v(72, -47) * mm, "end": v(69, -47) * mm, "construction": true});
            skLineSegment(sketch, "E8.left", {"start": v(72, -34) * mm, "end": v(72, -47) * mm});
            skLineSegment(sketch, "E8.right", {"start": v(69, -34) * mm, "end": v(69, -47) * mm});
            skLineSegment(sketch, "E9.1.0.0", {"start": v(62, -2) * mm, "end": v(62, -32) * mm});
            skLineSegment(sketch, "E9.1.0.1", {"start": v(62, -2) * mm, "end": v(59, -2) * mm});
            skLineSegment(sketch, "E9.1.0.2", {"start": v(59, -2) * mm, "end": v(59, -32) * mm});
            skLineSegment(sketch, "E9.1.0.3", {"start": v(62, -32) * mm, "end": v(59, -32) * mm});
            skLineSegment(sketch, "E9.1.0.4", {"start": v(62, -34) * mm, "end": v(59, -34) * mm});
            skLineSegment(sketch, "E9.1.0.5", {"start": v(62, -34) * mm, "end": v(62, -47) * mm});
            skLineSegment(sketch, "E9.1.0.6", {"start": v(62, -47) * mm, "end": v(59, -47) * mm, "construction": true});
            skLineSegment(sketch, "E9.1.0.7", {"start": v(59, -34) * mm, "end": v(59, -47) * mm});
            skLineSegment(sketch, "E9.2.0.0", {"start": v(52, -2) * mm, "end": v(52, -32) * mm});
            skLineSegment(sketch, "E9.2.0.1", {"start": v(52, -2) * mm, "end": v(49, -2) * mm});
            skLineSegment(sketch, "E9.2.0.2", {"start": v(49, -2) * mm, "end": v(49, -32) * mm});
            skLineSegment(sketch, "E9.2.0.3", {"start": v(52, -32) * mm, "end": v(49, -32) * mm});
            skLineSegment(sketch, "E9.2.0.4", {"start": v(52, -34) * mm, "end": v(49, -34) * mm});
            skLineSegment(sketch, "E9.2.0.5", {"start": v(52, -34) * mm, "end": v(52, -47) * mm});
            skLineSegment(sketch, "E9.2.0.6", {"start": v(52, -47) * mm, "end": v(49, -47) * mm, "construction": true});
            skLineSegment(sketch, "E9.2.0.7", {"start": v(49, -34) * mm, "end": v(49, -47) * mm});
            skLineSegment(sketch, "E9.3.0.0", {"start": v(42, -2) * mm, "end": v(42, -32) * mm});
            skLineSegment(sketch, "E9.3.0.1", {"start": v(42, -2) * mm, "end": v(39, -2) * mm});
            skLineSegment(sketch, "E9.3.0.2", {"start": v(39, -2) * mm, "end": v(39, -32) * mm});
            skLineSegment(sketch, "E9.3.0.3", {"start": v(42, -32) * mm, "end": v(39, -32) * mm});
            skLineSegment(sketch, "E9.3.0.4", {"start": v(42, -34) * mm, "end": v(39, -34) * mm});
            skLineSegment(sketch, "E9.3.0.5", {"start": v(42, -34) * mm, "end": v(42, -47) * mm});
            skLineSegment(sketch, "E9.3.0.6", {"start": v(42, -47) * mm, "end": v(39, -47) * mm, "construction": true});
            skLineSegment(sketch, "E9.3.0.7", {"start": v(39, -34) * mm, "end": v(39, -47) * mm});
            skLineSegment(sketch, "E9.4.0.0", {"start": v(32, -2) * mm, "end": v(32, -32) * mm});
            skLineSegment(sketch, "E9.4.0.1", {"start": v(32, -2) * mm, "end": v(29, -2) * mm});
            skLineSegment(sketch, "E9.4.0.2", {"start": v(29, -2) * mm, "end": v(29, -32) * mm});
            skLineSegment(sketch, "E9.4.0.3", {"start": v(32, -32) * mm, "end": v(29, -32) * mm});
            skLineSegment(sketch, "E9.4.0.4", {"start": v(32, -34) * mm, "end": v(29, -34) * mm});
            skLineSegment(sketch, "E9.4.0.5", {"start": v(32, -34) * mm, "end": v(32, -47) * mm});
            skLineSegment(sketch, "E9.4.0.6", {"start": v(32, -47) * mm, "end": v(29, -47) * mm, "construction": true});
            skLineSegment(sketch, "E9.4.0.7", {"start": v(29, -34) * mm, "end": v(29, -47) * mm});
            skLineSegment(sketch, "E9.5.0.0", {"start": v(22, -2) * mm, "end": v(22, -32) * mm});
            skLineSegment(sketch, "E9.5.0.1", {"start": v(22, -2) * mm, "end": v(19, -2) * mm});
            skLineSegment(sketch, "E9.5.0.2", {"start": v(19, -2) * mm, "end": v(19, -32) * mm});
            skLineSegment(sketch, "E9.5.0.3", {"start": v(22, -32) * mm, "end": v(19, -32) * mm});
            skLineSegment(sketch, "E9.5.0.4", {"start": v(22, -34) * mm, "end": v(19, -34) * mm});
            skLineSegment(sketch, "E9.5.0.5", {"start": v(22, -34) * mm, "end": v(22, -47) * mm});
            skLineSegment(sketch, "E9.5.0.6", {"start": v(22, -47) * mm, "end": v(19, -47) * mm, "construction": true});
            skLineSegment(sketch, "E9.5.0.7", {"start": v(19, -34) * mm, "end": v(19, -47) * mm});
            skLineSegment(sketch, "E9.6.0.0", {"start": v(12, -2) * mm, "end": v(12, -32) * mm});
            skLineSegment(sketch, "E9.6.0.1", {"start": v(12, -2) * mm, "end": v(9, -2) * mm});
            skLineSegment(sketch, "E9.6.0.2", {"start": v(9, -2) * mm, "end": v(9, -32) * mm});
            skLineSegment(sketch, "E9.6.0.3", {"start": v(12, -32) * mm, "end": v(9, -32) * mm});
            skLineSegment(sketch, "E9.6.0.4", {"start": v(12, -34) * mm, "end": v(9, -34) * mm});
            skLineSegment(sketch, "E9.6.0.5", {"start": v(12, -34) * mm, "end": v(12, -47) * mm});
            skLineSegment(sketch, "E9.6.0.6", {"start": v(12, -47) * mm, "end": v(9, -47) * mm, "construction": true});
            skLineSegment(sketch, "E9.6.0.7", {"start": v(9, -34) * mm, "end": v(9, -47) * mm});
            skLineSegment(sketch, "E9.7.0.0", {"start": v(2, -2) * mm, "end": v(2, -32) * mm});
            skLineSegment(sketch, "E9.7.0.1", {"start": v(2, -2) * mm, "end": v(-1, -2) * mm});
            skLineSegment(sketch, "E9.7.0.2", {"start": v(-1, -2) * mm, "end": v(-1, -32) * mm});
            skLineSegment(sketch, "E9.7.0.3", {"start": v(2, -32) * mm, "end": v(-1, -32) * mm});
            skLineSegment(sketch, "E9.7.0.4", {"start": v(2, -34) * mm, "end": v(-1, -34) * mm});
            skLineSegment(sketch, "E9.7.0.5", {"start": v(2, -34) * mm, "end": v(2, -47) * mm});
            skLineSegment(sketch, "E9.7.0.6", {"start": v(2, -47) * mm, "end": v(-1, -47) * mm, "construction": true});
            skLineSegment(sketch, "E9.7.0.7", {"start": v(-1, -34) * mm, "end": v(-1, -47) * mm});
            skLineSegment(sketch, "E9.8.0.0", {"start": v(-8, -2) * mm, "end": v(-8, -32) * mm});
            skLineSegment(sketch, "E9.8.0.1", {"start": v(-8, -2) * mm, "end": v(-11, -2) * mm});
            skLineSegment(sketch, "E9.8.0.2", {"start": v(-11, -2) * mm, "end": v(-11, -32) * mm});
            skLineSegment(sketch, "E9.8.0.3", {"start": v(-8, -32) * mm, "end": v(-11, -32) * mm});
            skLineSegment(sketch, "E9.8.0.4", {"start": v(-8, -34) * mm, "end": v(-11, -34) * mm});
            skLineSegment(sketch, "E9.8.0.5", {"start": v(-8, -34) * mm, "end": v(-8, -47) * mm});
            skLineSegment(sketch, "E9.8.0.6", {"start": v(-8, -47) * mm, "end": v(-11, -47) * mm, "construction": true});
            skLineSegment(sketch, "E9.8.0.7", {"start": v(-11, -34) * mm, "end": v(-11, -47) * mm});
            skLineSegment(sketch, "E9.9.0.0", {"start": v(-18, -2) * mm, "end": v(-18, -32) * mm});
            skLineSegment(sketch, "E9.9.0.1", {"start": v(-18, -2) * mm, "end": v(-21, -2) * mm});
            skLineSegment(sketch, "E9.9.0.2", {"start": v(-21, -2) * mm, "end": v(-21, -32) * mm});
            skLineSegment(sketch, "E9.9.0.3", {"start": v(-18, -32) * mm, "end": v(-21, -32) * mm});
            skLineSegment(sketch, "E9.9.0.4", {"start": v(-18, -34) * mm, "end": v(-21, -34) * mm});
            skLineSegment(sketch, "E9.9.0.5", {"start": v(-18, -34) * mm, "end": v(-18, -47) * mm});
            skLineSegment(sketch, "E9.9.0.6", {"start": v(-18, -47) * mm, "end": v(-21, -47) * mm, "construction": true});
            skLineSegment(sketch, "E9.9.0.7", {"start": v(-21, -34) * mm, "end": v(-21, -47) * mm});
            skLineSegment(sketch, "E9.10.0.0", {"start": v(-28, -2) * mm, "end": v(-28, -32) * mm});
            skLineSegment(sketch, "E9.10.0.1", {"start": v(-28, -2) * mm, "end": v(-31, -2) * mm});
            skLineSegment(sketch, "E9.10.0.2", {"start": v(-31, -2) * mm, "end": v(-31, -32) * mm});
            skLineSegment(sketch, "E9.10.0.3", {"start": v(-28, -32) * mm, "end": v(-31, -32) * mm});
            skLineSegment(sketch, "E9.10.0.4", {"start": v(-28, -34) * mm, "end": v(-31, -34) * mm});
            skLineSegment(sketch, "E9.10.0.5", {"start": v(-28, -34) * mm, "end": v(-28, -47) * mm});
            skLineSegment(sketch, "E9.10.0.6", {"start": v(-28, -47) * mm, "end": v(-31, -47) * mm, "construction": true});
            skLineSegment(sketch, "E9.10.0.7", {"start": v(-31, -34) * mm, "end": v(-31, -47) * mm});
            skLineSegment(sketch, "E9.11.0.0", {"start": v(-38, -2) * mm, "end": v(-38, -32) * mm});
            skLineSegment(sketch, "E9.11.0.1", {"start": v(-38, -2) * mm, "end": v(-41, -2) * mm});
            skLineSegment(sketch, "E9.11.0.2", {"start": v(-41, -2) * mm, "end": v(-41, -32) * mm});
            skLineSegment(sketch, "E9.11.0.3", {"start": v(-38, -32) * mm, "end": v(-41, -32) * mm});
            skLineSegment(sketch, "E9.11.0.4", {"start": v(-38, -34) * mm, "end": v(-41, -34) * mm});
            skLineSegment(sketch, "E9.11.0.5", {"start": v(-38, -34) * mm, "end": v(-38, -47) * mm});
            skLineSegment(sketch, "E9.11.0.6", {"start": v(-38, -47) * mm, "end": v(-41, -47) * mm, "construction": true});
            skLineSegment(sketch, "E9.11.0.7", {"start": v(-41, -34) * mm, "end": v(-41, -47) * mm});
            skLineSegment(sketch, "E9.12.0.0", {"start": v(-48, -2) * mm, "end": v(-48, -32) * mm});
            skLineSegment(sketch, "E9.12.0.1", {"start": v(-48, -2) * mm, "end": v(-51, -2) * mm});
            skLineSegment(sketch, "E9.12.0.2", {"start": v(-51, -2) * mm, "end": v(-51, -32) * mm});
            skLineSegment(sketch, "E9.12.0.3", {"start": v(-48, -32) * mm, "end": v(-51, -32) * mm});
            skLineSegment(sketch, "E9.12.0.4", {"start": v(-48, -34) * mm, "end": v(-51, -34) * mm});
            skLineSegment(sketch, "E9.12.0.5", {"start": v(-48, -34) * mm, "end": v(-48, -47) * mm});
            skLineSegment(sketch, "E9.12.0.6", {"start": v(-48, -47) * mm, "end": v(-51, -47) * mm, "construction": true});
            skLineSegment(sketch, "E9.12.0.7", {"start": v(-51, -34) * mm, "end": v(-51, -47) * mm});
            skLineSegment(sketch, "E9.13.0.0", {"start": v(-58, -2) * mm, "end": v(-58, -32) * mm});
            skLineSegment(sketch, "E9.13.0.1", {"start": v(-58, -2) * mm, "end": v(-61, -2) * mm});
            skLineSegment(sketch, "E9.13.0.2", {"start": v(-61, -2) * mm, "end": v(-61, -32) * mm});
            skLineSegment(sketch, "E9.13.0.3", {"start": v(-58, -32) * mm, "end": v(-61, -32) * mm});
            skLineSegment(sketch, "E9.13.0.4", {"start": v(-58, -34) * mm, "end": v(-61, -34) * mm});
            skLineSegment(sketch, "E9.13.0.5", {"start": v(-58, -34) * mm, "end": v(-58, -47) * mm});
            skLineSegment(sketch, "E9.13.0.6", {"start": v(-58, -47) * mm, "end": v(-61, -47) * mm, "construction": true});
            skLineSegment(sketch, "E9.13.0.7", {"start": v(-61, -34) * mm, "end": v(-61, -47) * mm});
            skLineSegment(sketch, "E9.14.0.0", {"start": v(-68, -2) * mm, "end": v(-68, -32) * mm});
            skLineSegment(sketch, "E9.14.0.1", {"start": v(-68, -2) * mm, "end": v(-71, -2) * mm});
            skLineSegment(sketch, "E9.14.0.2", {"start": v(-71, -2) * mm, "end": v(-71, -32) * mm});
            skLineSegment(sketch, "E9.14.0.3", {"start": v(-68, -32) * mm, "end": v(-71, -32) * mm});
            skLineSegment(sketch, "E9.14.0.4", {"start": v(-68, -34) * mm, "end": v(-71, -34) * mm});
            skLineSegment(sketch, "E9.14.0.5", {"start": v(-68, -34) * mm, "end": v(-68, -47) * mm});
            skLineSegment(sketch, "E9.14.0.6", {"start": v(-68, -47) * mm, "end": v(-71, -47) * mm, "construction": true});
            skLineSegment(sketch, "E9.14.0.7", {"start": v(-71, -34) * mm, "end": v(-71, -47) * mm});
            skLineSegment(sketch, "E10", {"start": v(-68, 47) * mm, "end": v(-68, 50) * mm});
            skLineSegment(sketch, "E11", {"start": v(-71, 47) * mm, "end": v(-71, 50) * mm});
            skLineSegment(sketch, "E12", {"start": v(-61, 47) * mm, "end": v(-61, 50) * mm});
            skLineSegment(sketch, "E13", {"start": v(-58.03, 47) * mm, "end": v(-58.03, 50) * mm});
            skLineSegment(sketch, "E14", {"start": v(-51, 47) * mm, "end": v(-51, 50) * mm});
            skLineSegment(sketch, "E15", {"start": v(-48, 47) * mm, "end": v(-48, 50) * mm});
            skLineSegment(sketch, "E16", {"start": v(-41, 47) * mm, "end": v(-41, 50) * mm});
            skLineSegment(sketch, "E17", {"start": v(-38, 47) * mm, "end": v(-38, 50) * mm});
            skLineSegment(sketch, "E18", {"start": v(-31, 47) * mm, "end": v(-31, 50) * mm});
            skLineSegment(sketch, "E19", {"start": v(-28, 47) * mm, "end": v(-28, 50) * mm});
            skLineSegment(sketch, "E20", {"start": v(-21, 47) * mm, "end": v(-21, 50) * mm});
            skLineSegment(sketch, "E21", {"start": v(-18, 47) * mm, "end": v(-18, 50) * mm});
            skLineSegment(sketch, "E22", {"start": v(-11, 47) * mm, "end": v(-11, 50) * mm});
            skLineSegment(sketch, "E23", {"start": v(-8, 47) * mm, "end": v(-8, 50) * mm});
            skLineSegment(sketch, "E24", {"start": v(-1, 47) * mm, "end": v(-1, 50) * mm});
            skLineSegment(sketch, "E25", {"start": v(2, 47) * mm, "end": v(2, 50) * mm});
            skLineSegment(sketch, "E26", {"start": v(9, 47) * mm, "end": v(9, 50) * mm});
            skLineSegment(sketch, "E27", {"start": v(12, 47) * mm, "end": v(12, 50) * mm});
            skLineSegment(sketch, "E28", {"start": v(19, 47) * mm, "end": v(19, 50) * mm});
            skLineSegment(sketch, "E29", {"start": v(22, 47) * mm, "end": v(22, 50) * mm});
            skLineSegment(sketch, "E30", {"start": v(29, 47) * mm, "end": v(29, 50) * mm});
            skLineSegment(sketch, "E31", {"start": v(32, 47) * mm, "end": v(32, 50) * mm});
            skLineSegment(sketch, "E32", {"start": v(39, 47) * mm, "end": v(39, 50) * mm});
            skLineSegment(sketch, "E33", {"start": v(42, 47) * mm, "end": v(42, 50) * mm});
            skLineSegment(sketch, "E34", {"start": v(49, 47) * mm, "end": v(49, 50) * mm});
            skLineSegment(sketch, "E35", {"start": v(52, 47) * mm, "end": v(52, 50) * mm});
            skLineSegment(sketch, "E36", {"start": v(59, 47) * mm, "end": v(59, 50) * mm});
            skLineSegment(sketch, "E37", {"start": v(62, 47) * mm, "end": v(62, 50) * mm});
            skLineSegment(sketch, "E38", {"start": v(69, 47) * mm, "end": v(69, 50) * mm});
            skLineSegment(sketch, "E39", {"start": v(72, 47) * mm, "end": v(72, 50) * mm});
            skLineSegment(sketch, "E40", {"start": v(-71, -47) * mm, "end": v(-71, -50) * mm});
            skLineSegment(sketch, "E41", {"start": v(-68, -47) * mm, "end": v(-68, -50) * mm});
            skLineSegment(sketch, "E42", {"start": v(-61, -47) * mm, "end": v(-61, -50) * mm});
            skLineSegment(sketch, "E43", {"start": v(-58, -47) * mm, "end": v(-58, -50) * mm});
            skLineSegment(sketch, "E44", {"start": v(-51, -47) * mm, "end": v(-51, -50) * mm});
            skLineSegment(sketch, "E45", {"start": v(-48, -47) * mm, "end": v(-48, -50) * mm});
            skLineSegment(sketch, "E46", {"start": v(-41, -47) * mm, "end": v(-41, -50) * mm});
            skLineSegment(sketch, "E47", {"start": v(-38, -47) * mm, "end": v(-38, -50) * mm});
            skLineSegment(sketch, "E48", {"start": v(-31, -47) * mm, "end": v(-31, -50) * mm});
            skLineSegment(sketch, "E49", {"start": v(-28, -47) * mm, "end": v(-28, -50) * mm});
            skLineSegment(sketch, "E50", {"start": v(-21, -47) * mm, "end": v(-21, -50) * mm});
            skLineSegment(sketch, "E51", {"start": v(-18, -47) * mm, "end": v(-18, -50) * mm});
            skLineSegment(sketch, "E52", {"start": v(-11, -47) * mm, "end": v(-11, -50) * mm});
            skLineSegment(sketch, "E53", {"start": v(-8, -47) * mm, "end": v(-8, -50) * mm});
            skLineSegment(sketch, "E54", {"start": v(-1, -47) * mm, "end": v(-1, -50) * mm});
            skLineSegment(sketch, "E55", {"start": v(2, -47) * mm, "end": v(2, -50) * mm});
            skLineSegment(sketch, "E56", {"start": v(9, -47) * mm, "end": v(9, -50) * mm});
            skLineSegment(sketch, "E57", {"start": v(12, -47) * mm, "end": v(12, -50) * mm});
            skLineSegment(sketch, "E58", {"start": v(19, -47) * mm, "end": v(19, -50) * mm});
            skLineSegment(sketch, "E59", {"start": v(22, -47) * mm, "end": v(22, -50) * mm});
            skLineSegment(sketch, "E60", {"start": v(29, -47) * mm, "end": v(29, -50) * mm});
            skLineSegment(sketch, "E61", {"start": v(32, -47) * mm, "end": v(32, -50) * mm});
            skLineSegment(sketch, "E62", {"start": v(39, -47) * mm, "end": v(39, -50) * mm});
            skLineSegment(sketch, "E63", {"start": v(42, -47) * mm, "end": v(42, -50) * mm});
            skLineSegment(sketch, "E64", {"start": v(52, -47) * mm, "end": v(52, -50) * mm});
            skLineSegment(sketch, "E65", {"start": v(59, -47) * mm, "end": v(59, -50) * mm});
            skLineSegment(sketch, "E66", {"start": v(62, -47) * mm, "end": v(62, -50) * mm});
            skLineSegment(sketch, "E67", {"start": v(69, -47) * mm, "end": v(69, -50) * mm});
            skLineSegment(sketch, "E68", {"start": v(72, -47) * mm, "end": v(72, -50) * mm});
            skLineSegment(sketch, "E69", {"start": v(49, -47) * mm, "end": v(49, -50) * mm});
            skLineSegment(sketch, "E70", {"start": v(-80, 50) * mm, "end": v(-100, 50) * mm});
            skLineSegment(sketch, "E71", {"start": v(-100, 50) * mm, "end": v(-100, -50) * mm});
            skLineSegment(sketch, "E72", {"start": v(-100, -50) * mm, "end": v(-80, -50) * mm});
            skLineSegment(sketch, "E73.MirrorCS", {"start": v(80, 50) * mm, "end": v(100, 50) * mm});
            skLineSegment(sketch, "E74.MirrorCS", {"start": v(100, 50) * mm, "end": v(100, -50) * mm});
            skLineSegment(sketch, "E75.MirrorCS", {"start": v(100, -50) * mm, "end": v(80, -50) * mm});
            skLineSegment(sketch, "E76", {"start": v(97, 50) * mm, "end": v(97, 30) * mm});
            skLineSegment(sketch, "E77", {"start": v(97, 30) * mm, "end": v(100, 30) * mm});
            skLineSegment(sketch, "E78", {"start": v(100, 10) * mm, "end": v(97, 10) * mm});
            skLineSegment(sketch, "E79", {"start": v(97, 10) * mm, "end": v(97, -10) * mm});
            skLineSegment(sketch, "E80", {"start": v(97, -10) * mm, "end": v(100, -10) * mm});
            skLineSegment(sketch, "E81.MirrorCS", {"start": v(97, -30) * mm, "end": v(100, -30) * mm});
            skLineSegment(sketch, "E82.MirrorCS", {"start": v(97, -50) * mm, "end": v(97, -30) * mm});
            skLineSegment(sketch, "E83.MirrorCS", {"start": v(-100, 10) * mm, "end": v(-97, 10) * mm});
            skLineSegment(sketch, "E84.MirrorCS", {"start": v(-97, 30) * mm, "end": v(-100, 30) * mm});
            skLineSegment(sketch, "E85.MirrorCS", {"start": v(-97, -30) * mm, "end": v(-100, -30) * mm});
            skLineSegment(sketch, "E86.MirrorCS", {"start": v(-97, -10) * mm, "end": v(-100, -10) * mm});
            skLineSegment(sketch, "E87.MirrorCS", {"start": v(-97, 10) * mm, "end": v(-97, -10) * mm});
            skLineSegment(sketch, "E88.MirrorCS", {"start": v(-97, 50) * mm, "end": v(-97, 30) * mm});
            skLineSegment(sketch, "E89.MirrorCS", {"start": v(-97, -50) * mm, "end": v(-97, -30) * mm});
            skSolve(sketch);
        }
        {
            var Q0;
            Q0=makeQuery(id+"F0.imprint","IMPRINT",FACE,{"disambiguationData":[TD([[makeQuery(id+"F0.imprint","IMPRINT",EDGE,{"derivedFrom":sQuery(id+"F0.wireOp",EDGE,"E0.bottom")}),1.0]])]});
            var Q1;
            {var subQ5=sQuery(id+"F0.wireOp",EDGE,"E0.right");Q1=makeQuery(id+"F0.imprint","IMPRINT",FACE,{"disambiguationData":[TD([[makeQuery(id+"F0.imprint","IMPRINT",EDGE,{"derivedFrom":subQ5}),-1.0]])]});}
            var Q2;
            {var subQ3=sQuery(id+"F0.wireOp",EDGE,"E0.left");Q2=makeQuery(id+"F0.imprint","IMPRINT",FACE,{"disambiguationData":[TD([[makeQuery(id+"F0.imprint","IMPRINT",EDGE,{"derivedFrom":subQ3}),1.0]])]});}
            extrude(context, id + "F1", {"entities" : qUnion([Q0, Q1, Q2]), "depth" : 3 * mm});
        }
    });
